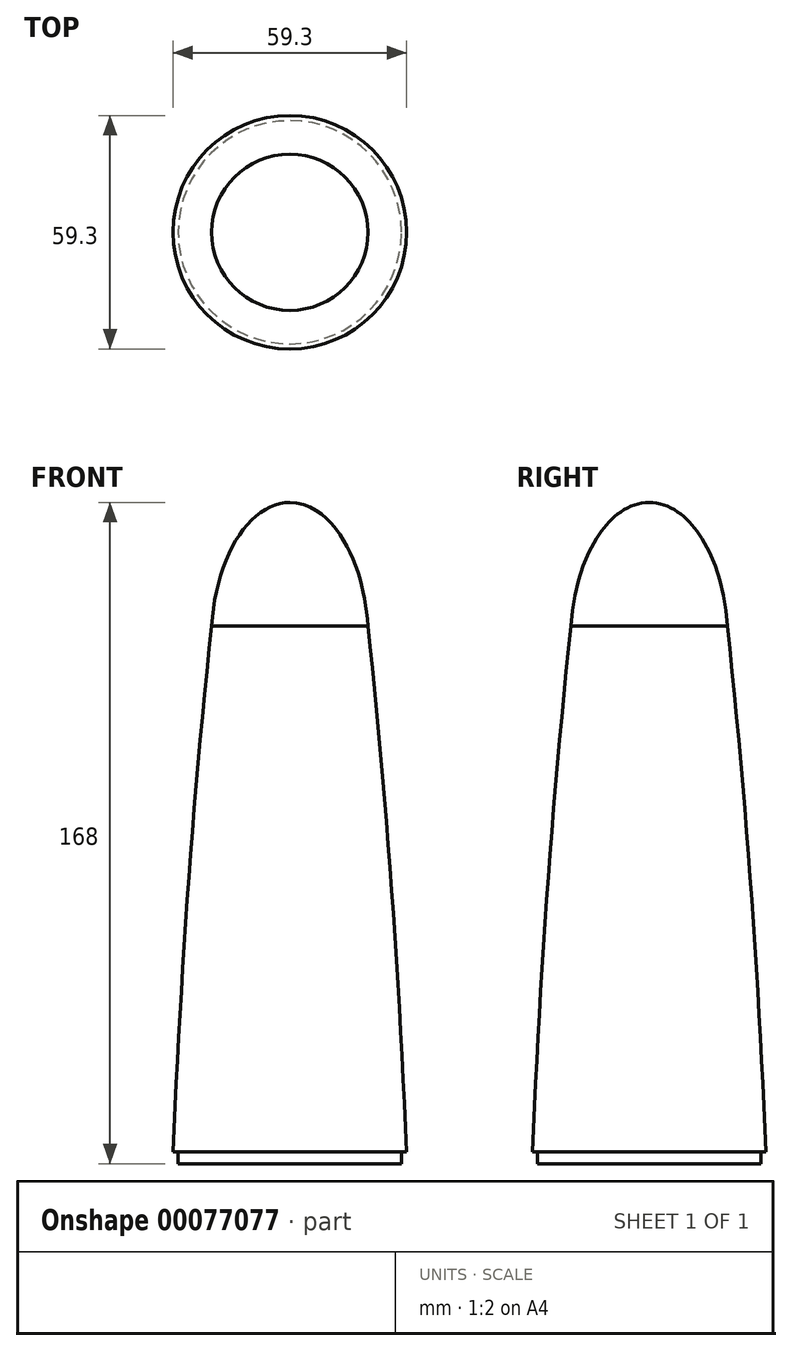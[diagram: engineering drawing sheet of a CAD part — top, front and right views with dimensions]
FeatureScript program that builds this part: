
annotation { "Feature Type Name" : "Feature", "Feature Type Description" : "" }
export const myFeature = defineFeature(function(context is Context, id is Id, definition is map)
    precondition{}
    {
        {
            var Q0;
            Q0=qCreatedBy(makeId("Front.planeOp"),FACE);
            var sketch = newSketch(context, id + "F0", { "sketchPlane" : qUnion([Q0])});
            skLineSegment(sketch, "E0", {"start": v(0, 294) * mm, "end": v(0, 253.7) * mm, "construction": true});
            skPoint(sketch, "E0.endSnap0", {"position": v(0, 294) * mm});
            skLineSegment(sketch, "E1.top", {"start": v(-28.36, 88.7) * mm, "end": v(-29.65, 88.7) * mm});
            skLineSegment(sketch, "E1.left", {"start": v(0, 253.7) * mm, "end": v(0, 88.7) * mm});
            skPoint(sketch, "E1.right.start.orphan", {"position": v(-63.28, 294) * mm});
            skPoint(sketch, "E2.orphan", {"position": v(-63.28, 88.7) * mm});
            skLineSegment(sketch, "E3.trimOffspring", {"start": v(0, 88.7) * mm, "end": v(0, 253.7) * mm});
            skPoint(sketch, "E4.orphan", {"position": v(0, 67.2) * mm});
            skLineSegment(sketch, "E5.top", {"start": v(0, 85.7) * mm, "end": v(-28.36, 85.7) * mm});
            skLineSegment(sketch, "E5.left", {"start": v(0, 88.7) * mm, "end": v(0, 85.7) * mm});
            skLineSegment(sketch, "E5.right", {"start": v(-28.36, 88.7) * mm, "end": v(-28.36, 85.7) * mm});
            skPoint(sketch, "E6.center.orphan", {"position": v(0, 0) * mm});
            skLineSegment(sketch, "E7", {"start": v(-12.1, 280.82) * mm, "end": v(-12.1, 280.82) * mm});
            skEllipticalArc(sketch, "E8", {});
            skLineSegment(sketch, "E9.trimOffspring", {"start": v(0, 291) * mm, "end": v(0, -294) * mm, "construction": true});
            skLineSegment(sketch, "E10", {"start": v(0, 291) * mm, "end": v(0, 85.7) * mm});
            skLineSegment(sketch, "E11.trimOffspring", {"start": v(0, 250.7) * mm, "end": v(0, 88.7) * mm, "construction": true});
            skEllipticalArc(sketch, "E12", {});
            const initialGuessF0  = {"E8": [0.005314983789743454, 0.06946444452614293, 0.035064994618088395, 0.9993850339846168, 0.29298721313299236, 0.03568930946230865, 1.0257646249616776, 1.5093101156219184], "E12": [0, 0.21825692057609558, 0, 1, 0.03544885802268982, 0.019991255425271946, 0, 1.455387067847335]};
            skSetInitialGuess(sketch, initialGuessF0);
            skSolve(sketch);
        }
        {
            var Q0;
            Q0=makeQuery(id+"F0.imprint","IMPRINT",FACE,{"disambiguationData":[TD([[makeQuery(id+"F0.imprint","IMPRINT",EDGE,{"derivedFrom":sQuery(id+"F0.wireOp",EDGE,"E1.top")}),-1.0]])]});
            var Q1;
            Q1=sQuery(id+"F0.wireOp",EDGE,"E0");
            revolve(context, id + "F1", {"entities" : qUnion([Q0]), "axis" : qUnion([Q1]), "revolveType" : RevolveType.FULL});
        }
        {
            var Q0;
            Q0=makeQuery(id+"F1.opRevolve","SWEPT_BODY",BODY,{"disambiguationData":[OSD([sQuery(id+"F0.wireOp",EDGE,"E1.top"),sQuery(id+"F0.wireOp",EDGE,"E3.trimOffspring"),sQuery(id+"F0.wireOp",EDGE,"E5.top"),sQuery(id+"F0.wireOp",EDGE,"E5.left"),sQuery(id+"F0.wireOp",EDGE,"E5.right"),sQuery(id+"F0.wireOp",EDGE,"988e126a-8830-41c9-8f9b-90423b33b9f4"),sQuery(id+"F0.wireOp",EDGE,"6f054b1e-dafb-45bf-af7e-3cf8252b6038")])]});
            transform(context, id + "F2", {"entities" : qUnion([Q0]), "transformType" : TransformType.TRANSLATION_3D, "dx" : 0 * mm, "dy" : 0 * mm, "dz" : -220 * mm, "makeCopy" : false});
        }
    });
